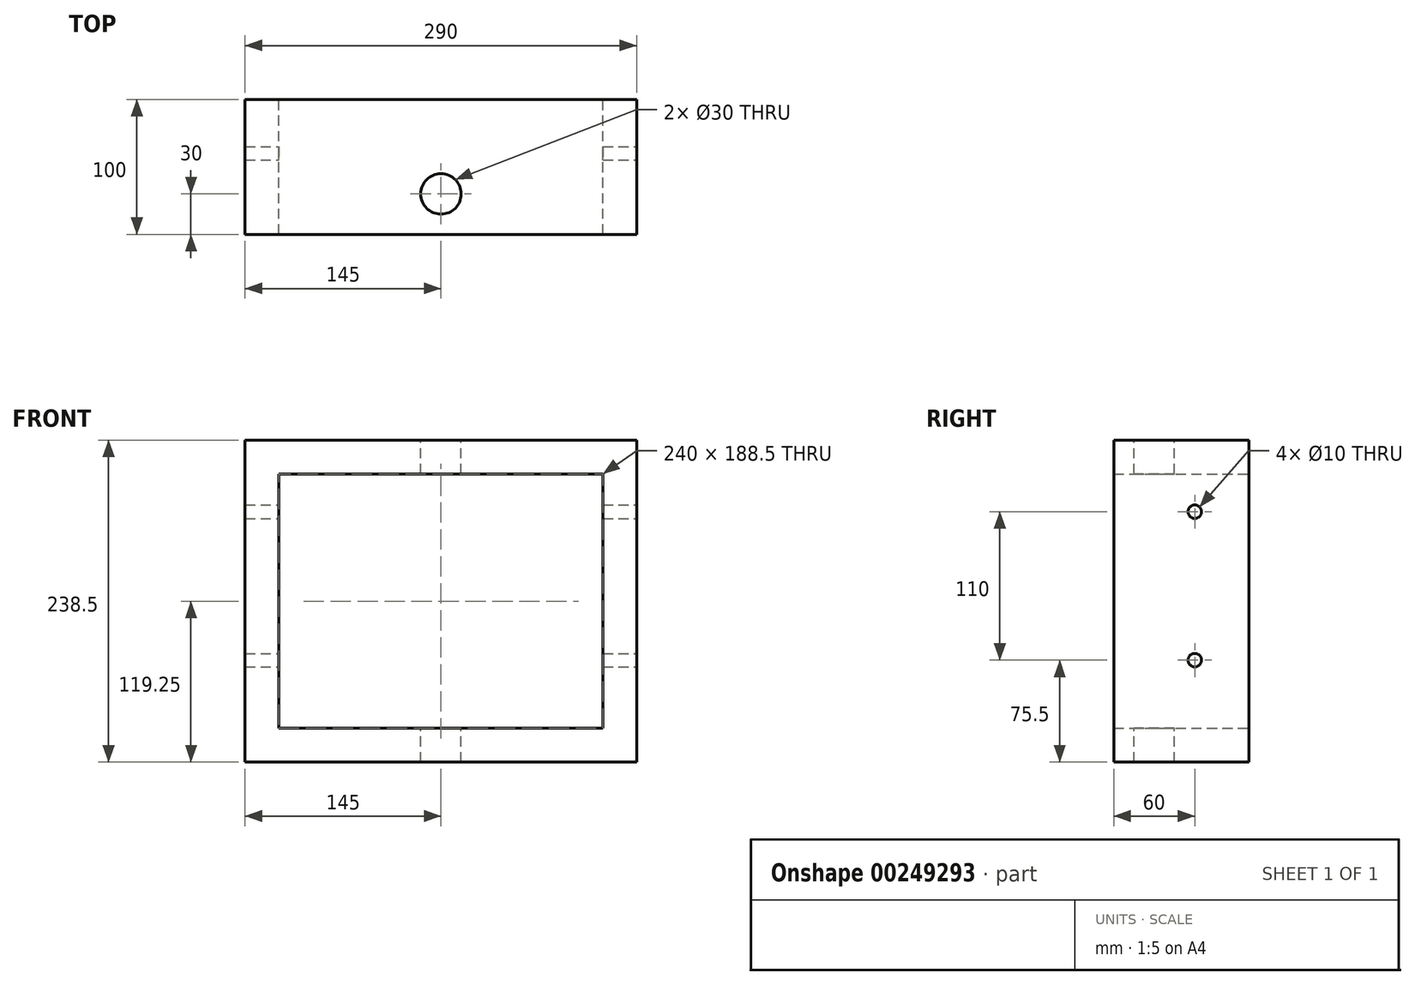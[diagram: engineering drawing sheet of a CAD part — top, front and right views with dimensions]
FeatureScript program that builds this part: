
annotation { "Feature Type Name" : "Feature", "Feature Type Description" : "" }
export const myFeature = defineFeature(function(context is Context, id is Id, definition is map)
    precondition{}
    {
        {
            var Q0;
            Q0=qCreatedBy(makeId("Front.planeOp"),FACE);
            var sketch = newSketch(context, id + "F0", { "sketchPlane" : qUnion([Q0])});
            skLineSegment(sketch, "E0.bottom", {"start": v(-120, 83) * mm, "end": v(120, 83) * mm});
            skLineSegment(sketch, "E0.top", {"start": v(-120, -105.5) * mm, "end": v(120, -105.5) * mm});
            skLineSegment(sketch, "E0.left", {"start": v(-120, 83) * mm, "end": v(-120, -105.5) * mm});
            skLineSegment(sketch, "E0.right", {"start": v(120, 83) * mm, "end": v(120, -105.5) * mm});
            skLineSegment(sketch, "E1.bottom", {"start": v(145, 108) * mm, "end": v(-145, 108) * mm});
            skLineSegment(sketch, "E1.left", {"start": v(145, 108) * mm, "end": v(145, -130.5) * mm});
            skLineSegment(sketch, "E1.right", {"start": v(-145, 108) * mm, "end": v(-145, -130.5) * mm});
            skPoint(sketch, "E1.middle", {"position": v(0, 0) * mm});
            skLineSegment(sketch, "E2", {"start": v(-145, -130.5) * mm, "end": v(145, -130.5) * mm});
            skPoint(sketch, "E3.orphan", {"position": v(-145, -108) * mm});
            skPoint(sketch, "E4.orphan", {"position": v(145, -108) * mm});
            skSolve(sketch);
        }
        {
            var Q0;
            Q0=makeQuery(id+"F0.imprint","IMPRINT",FACE,{"disambiguationData":[TD([[makeQuery(id+"F0.imprint","IMPRINT",EDGE,{"derivedFrom":sQuery(id+"F0.wireOp",EDGE,"E0.bottom")}),1.0]])]});
            extrude(context, id + "F1", {"entities" : qUnion([Q0]), "depth" : 100 * mm, "offsetDistance" : 25 * mm, "symmetric" : true});
        }
        {
            var Q0;
            Q0=makeQuery(id+"F1.opExtrude","SWEPT_FACE",FACE,{"disambiguationData":[OSD([sQuery(id+"F0.wireOp",EDGE,"E1.bottom")])]});
            var sketch = newSketch(context, id + "F2", { "sketchPlane" : qUnion([Q0])});
            skCircle(sketch, "E5", {"center": v(0, -20) * mm, "radius": 15 * mm});
            skSolve(sketch);
        }
        {
            var Q0;
            Q0=makeQuery(id+"F2.imprint","IMPRINT",FACE,{"disambiguationData":[TD([[makeQuery(id+"F2.imprint","IMPRINT",EDGE,{"derivedFrom":sQuery(id+"F2.wireOp",EDGE,"E5")}),1.0]])]});
            extrude(context, id + "F3", {"entities" : qUnion([Q0]), "operationType" : NewBodyOperationType.REMOVE, "endBound" : BoundingType.THROUGH_ALL, "oppositeDirection" : true, "depth" : 25 * mm, "offsetDistance" : 25 * mm});
        }
        {
            var Q0;
            Q0=makeQuery(id+"F1.opExtrude","SWEPT_FACE",FACE,{"disambiguationData":[OSD([sQuery(id+"F0.wireOp",EDGE,"E1.left")])]});
            var sketch = newSketch(context, id + "F4", { "sketchPlane" : qUnion([Q0])});
            skCircle(sketch, "E6", {"center": v(10, 55) * mm, "radius": 5 * mm});
            skCircle(sketch, "E7", {"center": v(10, -55) * mm, "radius": 5 * mm});
            skSolve(sketch);
        }
        {
            var Q0;
            Q0=makeQuery(id+"F4.imprint","IMPRINT",FACE,{"disambiguationData":[TD([[makeQuery(id+"F4.imprint","IMPRINT",EDGE,{"derivedFrom":sQuery(id+"F4.wireOp",EDGE,"E6")}),1.0]])]});
            var Q1;
            Q1=makeQuery(id+"F4.imprint","IMPRINT",FACE,{"disambiguationData":[TD([[makeQuery(id+"F4.imprint","IMPRINT",EDGE,{"derivedFrom":sQuery(id+"F4.wireOp",EDGE,"E7")}),1.0]])]});
            extrude(context, id + "F5", {"entities" : qUnion([Q0, Q1]), "operationType" : NewBodyOperationType.REMOVE, "endBound" : BoundingType.THROUGH_ALL, "oppositeDirection" : true, "depth" : 25 * mm, "offsetDistance" : 25 * mm});
        }
    });
